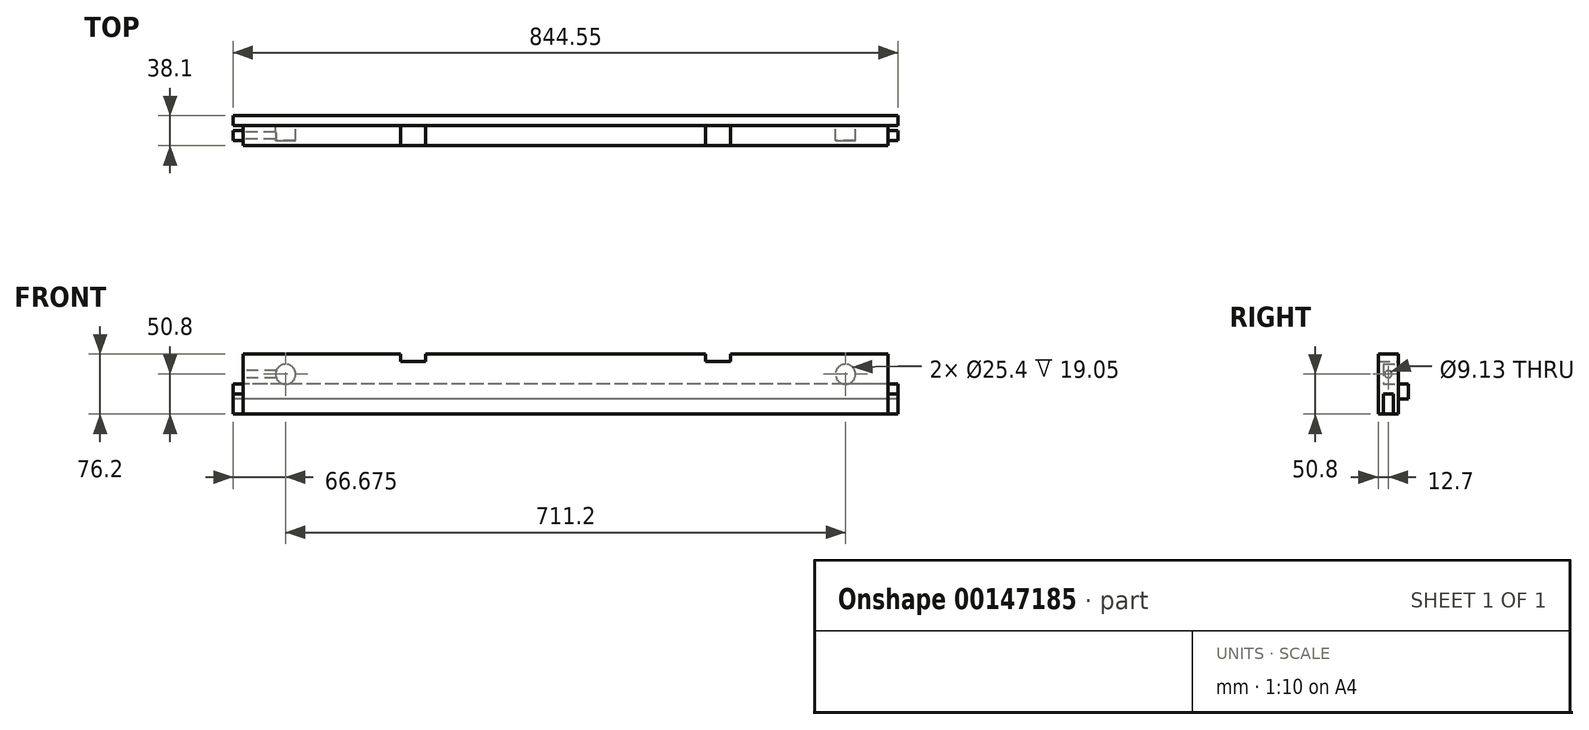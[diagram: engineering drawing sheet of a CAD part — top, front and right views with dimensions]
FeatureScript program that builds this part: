
annotation { "Feature Type Name" : "Feature", "Feature Type Description" : "" }
export const myFeature = defineFeature(function(context is Context, id is Id, definition is map)
    precondition{}
    {
        {
            var Q0;
            Q0=qCreatedBy(makeId("Front.planeOp"),FACE);
            var sketch = newSketch(context, id + "F0", { "sketchPlane" : qUnion([Q0])});
            skLineSegment(sketch, "E0.bottom", {"start": v(0, 0) * mm, "end": v(844.55, 0) * mm});
            skLineSegment(sketch, "E0.top", {"start": v(0, 76.2) * mm, "end": v(844.55, 76.2) * mm});
            skLineSegment(sketch, "E0.left", {"start": v(0, 0) * mm, "end": v(0, 76.2) * mm});
            skLineSegment(sketch, "E0.right", {"start": v(844.55, 0) * mm, "end": v(844.55, 76.2) * mm});
            skSolve(sketch);
        }
        {
            var Q0;
            Q0=makeQuery(id+"F0.imprint","IMPRINT",FACE,{"disambiguationData":[TD([[makeQuery(id+"F0.imprint","IMPRINT",EDGE,{"derivedFrom":sQuery(id+"F0.wireOp",EDGE,"E0.bottom")}),1.0]])]});
            extrude(context, id + "F1", {"entities" : qUnion([Q0]), "depth" : 25.4 * mm});
        }
        {
            var Q0;
            Q0=makeQuery(id+"F1.opExtrude","CAP_FACE",FACE,{"disambiguationData":[OSD([sQuery(id+"F0.wireOp",EDGE,"E0.bottom"),sQuery(id+"F0.wireOp",EDGE,"E0.top"),sQuery(id+"F0.wireOp",EDGE,"E0.left"),sQuery(id+"F0.wireOp",EDGE,"E0.right")])],"isStart":false});
            var sketch = newSketch(context, id + "F2", { "sketchPlane" : qUnion([Q0])});
            skLineSegment(sketch, "E1.bottom", {"start": v(0, 76.2) * mm, "end": v(12.7, 76.2) * mm});
            skLineSegment(sketch, "E1.top", {"start": v(0, 25.4) * mm, "end": v(12.7, 25.4) * mm});
            skLineSegment(sketch, "E1.left", {"start": v(0, 76.2) * mm, "end": v(0, 25.4) * mm});
            skLineSegment(sketch, "E1.right", {"start": v(12.7, 76.2) * mm, "end": v(12.7, 25.4) * mm});
            skLineSegment(sketch, "E2.bottom", {"start": v(831.85, 76.2) * mm, "end": v(844.55, 76.2) * mm});
            skLineSegment(sketch, "E2.top", {"start": v(831.85, 25.4) * mm, "end": v(844.55, 25.4) * mm});
            skLineSegment(sketch, "E2.left", {"start": v(831.85, 76.2) * mm, "end": v(831.85, 25.4) * mm});
            skLineSegment(sketch, "E2.right", {"start": v(844.55, 76.2) * mm, "end": v(844.55, 25.4) * mm});
            skSolve(sketch);
        }
        {
            var Q0;
            Q0=makeQuery(id+"F2.imprint","IMPRINT",FACE,{"disambiguationData":[TD([[makeQuery(id+"F2.imprint","IMPRINT",EDGE,{"derivedFrom":sQuery(id+"F2.wireOp",EDGE,"E1.bottom")}),-1.0]])]});
            var Q1;
            Q1=makeQuery(id+"F2.imprint","IMPRINT",FACE,{"disambiguationData":[TD([[makeQuery(id+"F2.imprint","IMPRINT",EDGE,{"derivedFrom":sQuery(id+"F2.wireOp",EDGE,"E2.bottom")}),-1.0]])]});
            extrude(context, id + "F3", {"entities" : qUnion([Q0, Q1]), "operationType" : NewBodyOperationType.REMOVE, "endBound" : BoundingType.THROUGH_ALL, "oppositeDirection" : true, "depth" : 25.4 * mm});
        }
        {
            var Q0;
            Q0=makeQuery(id+"F1.opExtrude","SWEPT_FACE",FACE,{"disambiguationData":[OSD([sQuery(id+"F0.wireOp",EDGE,"E0.bottom")])]});
            var sketch = newSketch(context, id + "F4", { "sketchPlane" : qUnion([Q0])});
            skLineSegment(sketch, "E3.bottom", {"start": v(0, 25.4) * mm, "end": v(12.7, 25.4) * mm});
            skLineSegment(sketch, "E3.top", {"start": v(0, 19.05) * mm, "end": v(12.7, 19.05) * mm});
            skLineSegment(sketch, "E3.left", {"start": v(0, 25.4) * mm, "end": v(0, 19.05) * mm});
            skLineSegment(sketch, "E3.right", {"start": v(12.7, 25.4) * mm, "end": v(12.7, 19.05) * mm});
            skLineSegment(sketch, "E4.bottom", {"start": v(831.85, 25.4) * mm, "end": v(844.55, 25.4) * mm});
            skLineSegment(sketch, "E4.top", {"start": v(831.85, 19.05) * mm, "end": v(844.55, 19.05) * mm});
            skLineSegment(sketch, "E4.left", {"start": v(831.85, 25.4) * mm, "end": v(831.85, 19.05) * mm});
            skLineSegment(sketch, "E4.right", {"start": v(844.55, 25.4) * mm, "end": v(844.55, 19.05) * mm});
            skLineSegment(sketch, "E5.bottom", {"start": v(0, 6.35) * mm, "end": v(12.7, 6.35) * mm});
            skLineSegment(sketch, "E5.top", {"start": v(0, 0) * mm, "end": v(12.7, 0) * mm});
            skLineSegment(sketch, "E5.left", {"start": v(0, 6.35) * mm, "end": v(0, 0) * mm});
            skLineSegment(sketch, "E5.right", {"start": v(12.7, 6.35) * mm, "end": v(12.7, 0) * mm});
            skLineSegment(sketch, "E6.bottom", {"start": v(831.85, 6.35) * mm, "end": v(844.55, 6.35) * mm});
            skLineSegment(sketch, "E6.top", {"start": v(831.85, 0) * mm, "end": v(844.55, 0) * mm});
            skLineSegment(sketch, "E6.left", {"start": v(831.85, 6.35) * mm, "end": v(831.85, 0) * mm});
            skLineSegment(sketch, "E6.right", {"start": v(844.55, 6.35) * mm, "end": v(844.55, 0) * mm});
            skSolve(sketch);
        }
        {
            var Q0;
            Q0=makeQuery(id+"F4.imprint","IMPRINT",FACE,{"disambiguationData":[TD([[makeQuery(id+"F4.imprint","IMPRINT",EDGE,{"derivedFrom":sQuery(id+"F4.wireOp",EDGE,"E4.bottom")}),-1.0]])]});
            var Q1;
            Q1=makeQuery(id+"F4.imprint","IMPRINT",FACE,{"disambiguationData":[TD([[makeQuery(id+"F4.imprint","IMPRINT",EDGE,{"derivedFrom":sQuery(id+"F4.wireOp",EDGE,"E6.bottom")}),-1.0]])]});
            var Q2;
            Q2=makeQuery(id+"F4.imprint","IMPRINT",FACE,{"disambiguationData":[TD([[makeQuery(id+"F4.imprint","IMPRINT",EDGE,{"derivedFrom":sQuery(id+"F4.wireOp",EDGE,"E3.bottom")}),-1.0]])]});
            var Q3;
            Q3=makeQuery(id+"F4.imprint","IMPRINT",FACE,{"disambiguationData":[TD([[makeQuery(id+"F4.imprint","IMPRINT",EDGE,{"derivedFrom":sQuery(id+"F4.wireOp",EDGE,"E5.bottom")}),-1.0]])]});
            extrude(context, id + "F5", {"entities" : qUnion([Q0, Q1, Q2, Q3]), "operationType" : NewBodyOperationType.REMOVE, "endBound" : BoundingType.THROUGH_ALL, "oppositeDirection" : true, "depth" : 25.4 * mm});
        }
        {
            var Q0;
            Q0=makeQuery(id+"F5.boolean.opBoolean","MERGE",FACE,{"derivedFrom":[makeQuery(id+"F3.boolean.opBoolean","COPY",FACE,{"derivedFrom":makeQuery(id+"F3.opExtrude","SWEPT_FACE",FACE,{"disambiguationData":[OSD([sQuery(id+"F2.wireOp",EDGE,"E1.right")])]})}),makeQuery(id+"F5.opExtrude","SWEPT_FACE",FACE,{"disambiguationData":[OSD([sQuery(id+"F4.wireOp",EDGE,"E3.right")])]}),makeQuery(id+"F5.opExtrude","SWEPT_FACE",FACE,{"disambiguationData":[OSD([sQuery(id+"F4.wireOp",EDGE,"E5.right")])]})]});
            var sketch = newSketch(context, id + "F6", { "sketchPlane" : qUnion([Q0])});
            skCircle(sketch, "E7", {"center": v(12.7, 50.8) * mm, "radius": 4.56 * mm});
            skPoint(sketch, "E7.centerSnap0", {"position": v(12.7, 76.2) * mm});
            skSolve(sketch);
        }
        {
            var Q0;
            Q0=makeQuery(id+"F6.imprint","IMPRINT",FACE,{"disambiguationData":[TD([[makeQuery(id+"F6.imprint","IMPRINT",EDGE,{"derivedFrom":sQuery(id+"F6.wireOp",EDGE,"E7")}),1.0]])]});
            extrude(context, id + "F7", {"entities" : qUnion([Q0]), "operationType" : NewBodyOperationType.REMOVE, "oppositeDirection" : true, "depth" : 50.8 * mm});
        }
        {
            var Q0;
            Q0=makeQuery(id+"F1.opExtrude","CAP_FACE",FACE,{"disambiguationData":[OSD([sQuery(id+"F0.wireOp",EDGE,"E0.bottom"),sQuery(id+"F0.wireOp",EDGE,"E0.top"),sQuery(id+"F0.wireOp",EDGE,"E0.left"),sQuery(id+"F0.wireOp",EDGE,"E0.right")])],"isStart":true});
            var sketch = newSketch(context, id + "F8", { "sketchPlane" : qUnion([Q0])});
            skCircle(sketch, "E8", {"center": v(-66.67, 50.8) * mm, "radius": 12.7 * mm});
            skCircle(sketch, "E9", {"center": v(-777.88, 50.8) * mm, "radius": 12.7 * mm});
            skSolve(sketch);
        }
        {
            var Q0;
            Q0=makeQuery(id+"F8.imprint","IMPRINT",FACE,{"disambiguationData":[TD([[makeQuery(id+"F8.imprint","IMPRINT",EDGE,{"derivedFrom":sQuery(id+"F8.wireOp",EDGE,"E8")}),1.0]])]});
            var Q1;
            Q1=makeQuery(id+"F8.imprint","IMPRINT",FACE,{"disambiguationData":[TD([[makeQuery(id+"F8.imprint","IMPRINT",EDGE,{"derivedFrom":sQuery(id+"F8.wireOp",EDGE,"E9")}),1.0]])]});
            extrude(context, id + "F9", {"entities" : qUnion([Q0, Q1]), "operationType" : NewBodyOperationType.REMOVE, "oppositeDirection" : true, "depth" : 19.05 * mm});
        }
        {
            var Q0;
            Q0=makeQuery(id+"F1.opExtrude","CAP_FACE",FACE,{"disambiguationData":[OSD([sQuery(id+"F0.wireOp",EDGE,"E0.bottom"),sQuery(id+"F0.wireOp",EDGE,"E0.top"),sQuery(id+"F0.wireOp",EDGE,"E0.left"),sQuery(id+"F0.wireOp",EDGE,"E0.right")])],"isStart":true});
            var sketch = newSketch(context, id + "F10", { "sketchPlane" : qUnion([Q0])});
            skLineSegment(sketch, "E10.bottom", {"start": v(-844.55, 38.1) * mm, "end": v(0, 38.1) * mm});
            skLineSegment(sketch, "E10.top", {"start": v(-844.55, 19.05) * mm, "end": v(0, 19.05) * mm});
            skLineSegment(sketch, "E10.left", {"start": v(-844.55, 38.1) * mm, "end": v(-844.55, 19.05) * mm});
            skLineSegment(sketch, "E10.right", {"start": v(0, 38.1) * mm, "end": v(0, 19.05) * mm});
            skSolve(sketch);
        }
        {
            var Q0;
            Q0=makeQuery(id+"F10.imprint","IMPRINT",FACE,{"disambiguationData":[TD([[makeQuery(id+"F10.imprint","IMPRINT",EDGE,{"derivedFrom":sQuery(id+"F10.wireOp",EDGE,"E10.bottom")}),-1.0]])]});
            var Q1;
            {var subQ0=sQuery(id+"F10.wireOp",EDGE,"E10.left");Q1=makeQuery(id+"F10.imprint","IMPRINT",FACE,{"disambiguationData":[TD([[makeQuery(id+"F10.imprint","IMPRINT",EDGE,{"derivedFrom":subQ0}),1.0]])]});}
            var Q2;
            {var subQ0=sQuery(id+"F10.wireOp",EDGE,"E10.right");Q2=makeQuery(id+"F10.imprint","IMPRINT",FACE,{"disambiguationData":[TD([[makeQuery(id+"F10.imprint","IMPRINT",EDGE,{"derivedFrom":subQ0}),-1.0]])]});}
            extrude(context, id + "F11", {"entities" : qUnion([Q0, Q1, Q2]), "operationType" : NewBodyOperationType.ADD, "depth" : 12.7 * mm});
        }
        {
            var Q0;
            Q0=makeQuery(id+"F1.opExtrude","SWEPT_FACE",FACE,{"disambiguationData":[OSD([sQuery(id+"F0.wireOp",EDGE,"E0.top")])]});
            var sketch = newSketch(context, id + "F12", { "sketchPlane" : qUnion([Q0])});
            skLineSegment(sketch, "E11.bottom", {"start": v(212.72, -25.4) * mm, "end": v(244.47, -25.4) * mm});
            skLineSegment(sketch, "E11.top", {"start": v(212.72, 0) * mm, "end": v(244.47, 0) * mm});
            skLineSegment(sketch, "E11.left", {"start": v(212.72, -25.4) * mm, "end": v(212.72, 0) * mm});
            skLineSegment(sketch, "E11.right", {"start": v(244.47, -25.4) * mm, "end": v(244.47, 0) * mm});
            skLineSegment(sketch, "E12.bottom", {"start": v(600.08, -25.4) * mm, "end": v(631.83, -25.4) * mm});
            skLineSegment(sketch, "E12.top", {"start": v(600.08, 0) * mm, "end": v(631.83, 0) * mm});
            skLineSegment(sketch, "E12.left", {"start": v(600.08, -25.4) * mm, "end": v(600.08, 0) * mm});
            skLineSegment(sketch, "E12.right", {"start": v(631.83, -25.4) * mm, "end": v(631.83, 0) * mm});
            skSolve(sketch);
        }
        {
            var Q0;
            Q0=makeQuery(id+"F12.imprint","IMPRINT",FACE,{"disambiguationData":[TD([[makeQuery(id+"F12.imprint","IMPRINT",EDGE,{"derivedFrom":sQuery(id+"F12.wireOp",EDGE,"E11.bottom")}),1.0]])]});
            var Q1;
            Q1=makeQuery(id+"F12.imprint","IMPRINT",FACE,{"disambiguationData":[TD([[makeQuery(id+"F12.imprint","IMPRINT",EDGE,{"derivedFrom":sQuery(id+"F12.wireOp",EDGE,"E12.bottom")}),1.0]])]});
            extrude(context, id + "F13", {"entities" : qUnion([Q0, Q1]), "operationType" : NewBodyOperationType.REMOVE, "oppositeDirection" : true, "depth" : 9.52 * mm});
        }
    });
